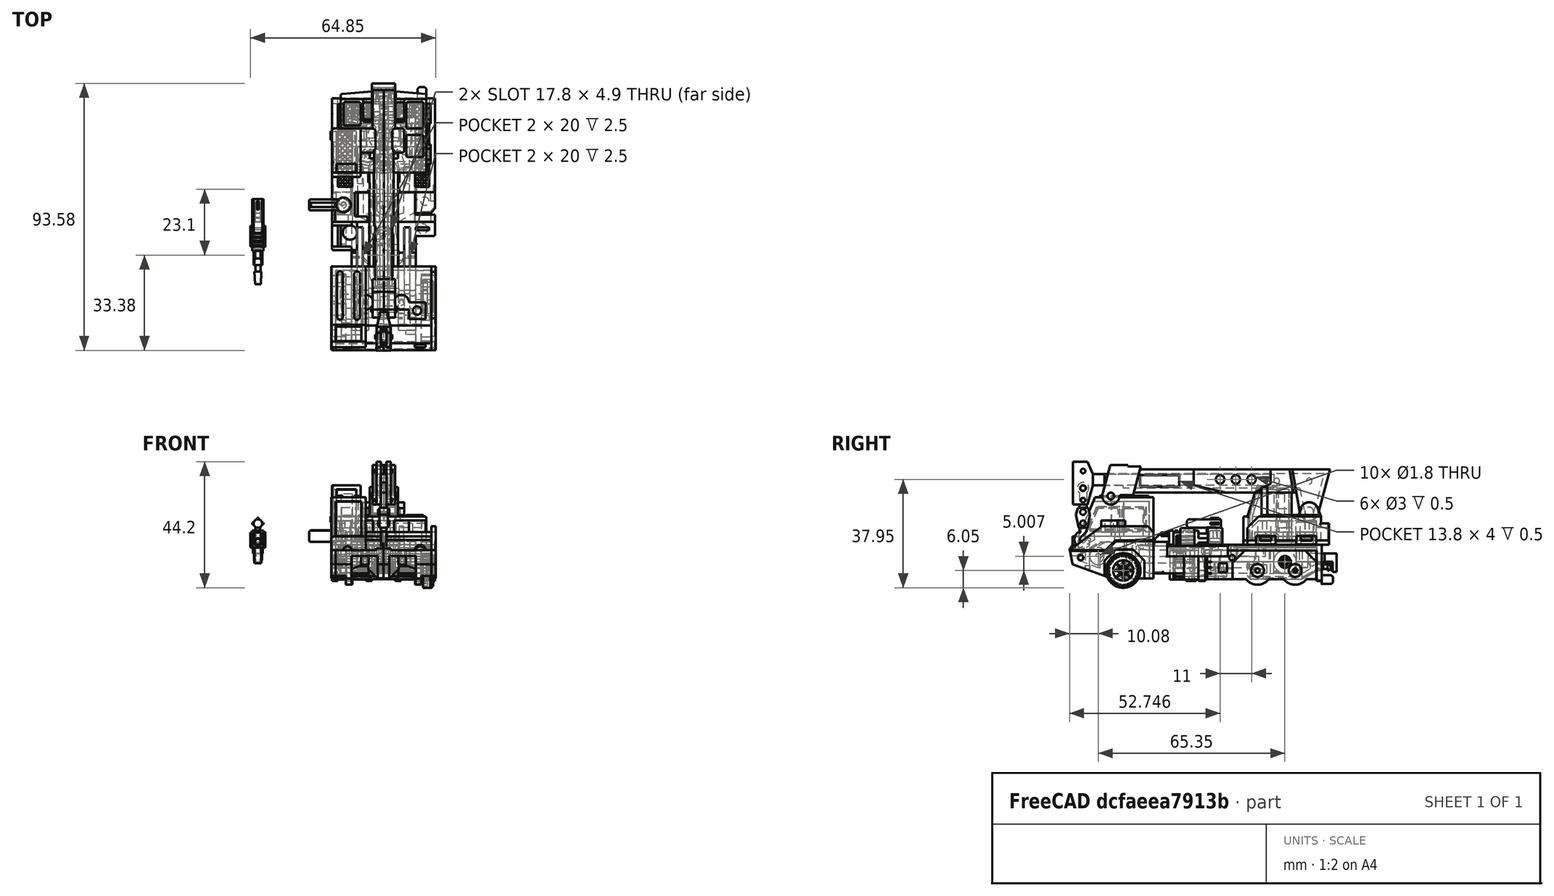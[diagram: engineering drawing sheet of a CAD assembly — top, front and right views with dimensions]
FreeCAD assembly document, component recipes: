
FREECAD ASSEMBLY — COMPONENT RECIPES ("Hook")

This assembly document has 27 components, labeled P0..P26 below (a component is one placed body or linked part). 27 of them carry a construction recipe — the FreeCAD feature program that regenerates the part from scratch, quoted from this document or its linked companion documents; the rest are supplied as boundary geometry only. No exploded tour is included for this assembly.
NOTE — document 5 of 5 of this assembly tour. The two overview renders and the header above are repeated from document 1; the component sections below continue where the previous document stopped.
COMPONENT P26 — recipe-attached ("Head", modeled in this document).
Construction recipe (the document's own serialized feature program — sketch geometry with constraints, then the solid features built on it; lengths are millimeters unless a unit is written):

FEATURE [Sketcher::SketchObject] Sketch190
  ArcFitTolerance = 1e-06
  AttachmentSupport = -> [XY_Plane013]
  FullyConstrained = true
  MakeInternals = false
  MapMode = 5
  sketch-geometry (4):
    g0: LineSegment StartX=0 StartY=0 StartZ=0 EndX=8 EndY=0 EndZ=0
    g1: LineSegment StartX=8 StartY=0 StartZ=0 EndX=8 EndY=10 EndZ=0
    g2: LineSegment StartX=8 StartY=10 StartZ=0 EndX=0 EndY=10 EndZ=0
    g3: LineSegment StartX=0 StartY=10 StartZ=0 EndX=0 EndY=0 EndZ=0
  constraints (11):
    c: Coincident(g0,g1)
    c: Coincident(g1,g2)
    c: Coincident(g2,g3)
    c: Coincident(g3,g0)
    c: Horizontal(g0)
    c: Horizontal(g2)
    c: Vertical(g1)
    c: Vertical(g3)
    c: Coincident(g0,g-1)
    c: DistanceX(g2,g2) = 8
    c: DistanceY(g3,g3) = 10
FEATURE [PartDesign::Pad] Pad127
  Direction = (0,0,1)
  Length = 3.5
  Length2 = 10
  Profile = -> Sketch190
  ReferenceAxis = -> Sketch190 [N_Axis]
  Refine = true
  Suppressed = false
  Type = 0
FEATURE [Sketcher::SketchObject] Sketch191
  ArcFitTolerance = 1e-06
  AttachmentSupport = -> [Pad127]
  ExternalGeometry = -> [Pad127]
  FullyConstrained = true
  MakeInternals = false
  MapMode = 5
  Placement = pos=(0,0,0) rot=(1,0,0;3.14159rad)
  sketch-geometry (4):
    g0: LineSegment StartX=0 StartY=0 StartZ=0 EndX=0 EndY=-1.4 EndZ=0
    g1: LineSegment StartX=0 StartY=-1.4 StartZ=0 EndX=8 EndY=-1.4 EndZ=0
    g2: LineSegment StartX=8 StartY=-1.4 StartZ=0 EndX=8 EndY=0 EndZ=0
    g3: LineSegment StartX=8 StartY=0 StartZ=0 EndX=0 EndY=0 EndZ=0
  constraints (11):
    c: Coincident(g0,g1)
    c: Coincident(g1,g2)
    c: Coincident(g2,g3)
    c: Coincident(g3,g0)
    c: Vertical(g0)
    c: Vertical(g2)
    c: Horizontal(g1)
    c: Horizontal(g3)
    c: Coincident(g0,g-1)
    c: PointOnObject(g1,g-3)
    c: DistanceY(g0,g0) = 1.4
FEATURE [PartDesign::Pad] Pad128
  BaseFeature = -> Pad127
  Direction = (0,0,-1)
  Length = 3.5
  Length2 = 10
  Profile = -> Sketch191
  ReferenceAxis = -> Sketch191 [N_Axis]
  Refine = true
  Suppressed = false
  Type = 0
FEATURE [Sketcher::SketchObject] Sketch192
  ArcFitTolerance = 1e-06
  AttachmentSupport = -> [Pad128]
  ExternalGeometry = -> [Pad128]
  FullyConstrained = true
  MakeInternals = false
  MapMode = 5
  Placement = pos=(0,0,0) rot=(0.57735,-0.57735,-0.57735;2.0944rad)
  sketch-geometry (2):
    g0: ArcOfCircle CenterX=-8.65 CenterY=0 CenterZ=0 NormalX=0 NormalY=0 NormalZ=1 AngleXU=0 Radius=1.35 StartAngle=0 EndAngle=3.14159
    g1: LineSegment StartX=-10 StartY=2e-16 StartZ=0 EndX=-7.3 EndY=0 EndZ=0
  constraints (6):
    c: Coincident(g0,g-4)
    c: PointOnObject(g0,g-4)
    c: PointOnObject(g0,g-4)
    c: Diameter(g0) = 2.7
    c: Coincident(g1,g0)
    c: Coincident(g1,g0)
FEATURE [PartDesign::Pad] Pad129
  BaseFeature = -> Pad128
  Direction = (-1,0,0)
  Length = 1.8
  Length2 = 10
  Profile = -> Sketch192
  ReferenceAxis = -> Sketch192 [N_Axis]
  Refine = true
  Suppressed = false
  Type = 0
FEATURE [Sketcher::SketchObject] Sketch193
  ArcFitTolerance = 1e-06
  AttachmentSupport = -> [Pad129]
  ExternalGeometry = -> [Pad129]
  FullyConstrained = true
  MakeInternals = false
  MapMode = 5
  Placement = pos=(8,0,0) rot=(0.57735,0.57735,0.57735;2.0944rad)
  sketch-geometry (2):
    g0: ArcOfCircle CenterX=8.65 CenterY=0 CenterZ=0 NormalX=0 NormalY=0 NormalZ=1 AngleXU=0 Radius=1.35 StartAngle=0 EndAngle=3.14159
    g1: LineSegment StartX=7.3 StartY=2e-16 StartZ=0 EndX=10 EndY=0 EndZ=0
  constraints (6):
    c: Coincident(g0,g-4)
    c: PointOnObject(g0,g-4)
    c: PointOnObject(g0,g-4)
    c: Coincident(g1,g0)
    c: Coincident(g1,g0)
    c: Diameter(g0) = 2.7
FEATURE [PartDesign::Pad] Pad130
  BaseFeature = -> Pad129
  Direction = (1,0,0)
  Length = 1.8
  Length2 = 10
  Profile = -> Sketch193
  ReferenceAxis = -> Sketch193 [N_Axis]
  Refine = true
  Suppressed = false
  Type = 0
FEATURE [PartDesign::Pocket] Pocket088
  BaseFeature = -> Pad130
  Direction = (0,0,-1)
  Length = 0.5
  Length2 = 5
  Profile = -> Pad130 [Face1]
  Refine = true
  Suppressed = false
  Type = 0
FEATURE [PartDesign::Pad] Pad131
  BaseFeature = -> Pocket088
  Direction = (-1,0,0)
  Length = 0.1
  Length2 = 10
  Profile = -> Pocket088 [Face2]
  Refine = true
  Suppressed = false
  Type = 0
FEATURE [PartDesign::Pad] Pad132
  BaseFeature = -> Pad131
  Direction = (1,0,0)
  Length = 0.1
  Length2 = 10
  Profile = -> Pad131 [Face5]
  Refine = true
  Suppressed = false
  Type = 0
FEATURE [Sketcher::SketchObject] Sketch195
  ArcFitTolerance = 1e-06
  AttachmentOffset = pos=(0,0,-2.2) rot=(0,0,1;0rad)
  AttachmentSupport = -> [Pad132]
  ExternalGeometry = -> [Pad132]
  FullyConstrained = true
  MakeInternals = false
  MapMode = 5
  Placement = pos=(0.4,0,0) rot=(0.57735,-0.57735,-0.57735;2.0944rad)
  sketch-geometry (2):
    g0: LineSegment StartX=-10 StartY=5.6939e-12 StartZ=0 EndX=-7.3 EndY=5.694e-12 EndZ=0
    g1: ArcOfCircle CenterX=-8.65 CenterY=1e-16 CenterZ=0 NormalX=0 NormalY=0 NormalZ=1 AngleXU=0 Radius=1.35 StartAngle=3.14159 EndAngle=6.28319
  constraints (5):
    c: Coincident(g0,g-3)
    c: Coincident(g0,g-3)
    c: Coincident(g1,g0)
    c: Coincident(g1,g0)
    c: PointOnObject(g1,g0)
FEATURE [PartDesign::Pad] Pad133
  BaseFeature = -> Pad132
  Direction = (-1,0,0)
  Length = 7.2
  Length2 = 10
  Profile = -> Sketch195
  ReferenceAxis = -> Sketch195 [N_Axis]
  Refine = true
  Reversed = true
  Suppressed = false
  Type = 0
FEATURE [Sketcher::SketchObject] Sketch196
  ArcFitTolerance = 1e-06
  AttachmentSupport = -> [Pad133]
  ExternalGeometry = -> [Pad133]
  FullyConstrained = true
  MakeInternals = false
  MapMode = 5
  Placement = pos=(0,0,0) rot=(1,0,0;3.14159rad)
  sketch-geometry (16):
    g0: LineSegment StartX=6.3 StartY=-6.73887 StartZ=0 EndX=6.3 EndY=-3.23887 EndZ=0
    g1: LineSegment StartX=6.3 StartY=-3.23887 StartZ=0 EndX=7.64681 EndY=-3.56312 EndZ=0
    g2: LineSegment StartX=7.8 StartY=-3.75756 StartZ=0 EndX=7.8 EndY=-5.95756 EndZ=0
    g3: LineSegment StartX=7.67952 StartY=-6.14107 StartZ=0 EndX=6.3 EndY=-6.73887 EndZ=0
    g4: ArcOfCircle CenterX=7.6 CenterY=-5.95756 CenterZ=0 NormalX=0 NormalY=0 NormalZ=1 AngleXU=0 Radius=0.2 StartAngle=5.1213 EndAngle=6.28319
    g5: GeomPoint [constr] X=7.8 Y=-6.08887 Z=0
    g6: ArcOfCircle CenterX=7.6 CenterY=-3.75756 CenterZ=0 NormalX=0 NormalY=0 NormalZ=1 AngleXU=0 Radius=0.2 StartAngle=1e-16 EndAngle=1.33454
    g7: GeomPoint [constr] X=7.8 Y=-3.6 Z=0
    g8: LineSegment StartX=1.7 StartY=-3.23887 StartZ=0 EndX=1.7 EndY=-6.73887 EndZ=0
    g9: LineSegment StartX=1.7 StartY=-6.73887 StartZ=0 EndX=0.320479 EndY=-6.14107 EndZ=0
    g10: LineSegment StartX=0.2 StartY=-5.95756 StartZ=0 EndX=0.2 EndY=-3.75756 EndZ=0
    g11: LineSegment StartX=0.353187 StartY=-3.56312 StartZ=0 EndX=1.7 EndY=-3.23887 EndZ=0
    g12: ArcOfCircle CenterX=0.4 CenterY=-5.95756 CenterZ=0 NormalX=0 NormalY=0 NormalZ=1 AngleXU=0 Radius=0.2 StartAngle=3.14159 EndAngle=4.30348
    g13: GeomPoint [constr] X=0.2 Y=-6.08887 Z=0
    g14: ArcOfCircle CenterX=0.4 CenterY=-3.75756 CenterZ=0 NormalX=0 NormalY=0 NormalZ=1 AngleXU=0 Radius=0.2 StartAngle=1.80706 EndAngle=3.14159
    g15: GeomPoint [constr] X=0.2 Y=-3.6 Z=0
  constraints (40):
    c: Vertical(g0)
    c: Coincident(g1,g0)
    c: Vertical(g2)
    c: Coincident(g3,g0)
    c: PointOnObject(g5,g2)
    c: PointOnObject(g5,g3)
    c: Tangent(g2,g4) = 1.5708
    c: Tangent(g3,g4) = 1.5708
    c: PointOnObject(g7,g1)
    c: PointOnObject(g7,g2)
    c: Tangent(g1,g6) = 1.5708
    c: Tangent(g2,g6) = 1.5708
    c: DistanceY(g0,g0) = 3.5
    c: DistanceY(g2,g2) = 2.2
    c: Radius(g4) = 0.2
    c: Radius(g6) = 0.2
    c: DistanceY(g0,g5) = 0.65
    c: DistanceX(g0,g2) = 1.5
    c: DistanceX(g2,g-3) = 0.3
    c: DistanceY(g7,g-3) = 2.2
    c: Vertical(g8)
    c: Coincident(g9,g8)
    c: Vertical(g10)
    c: Coincident(g11,g8)
    c: DistanceY(g8,g8) = 3.5
    c: PointOnObject(g13,g9)
    c: PointOnObject(g13,g10)
    c: Tangent(g9,g12) = 1.5708
    c: Tangent(g10,g12) = 1.5708
    c: PointOnObject(g15,g10)
    c: PointOnObject(g15,g11)
    c: Tangent(g10,g14) = 1.5708
    c: Tangent(g11,g14) = 1.5708
    c: DistanceX(g-4,g10) = 0.3
    c: Radius(g14) = 0.2
    c: Radius(g12) = 0.2
    c: DistanceX(g10,g8) = 1.5
    c: DistanceY(g8,g13) = 0.65
    c: DistanceY(g15,g-4) = 2.2
    c: DistanceY(g10,g10) = 2.2
FEATURE [PartDesign::Pad] Pad134
  BaseFeature = -> Pad133
  Direction = (0,0,-1)
  Length = 0.8
  Length2 = 10
  Profile = -> Sketch196
  ReferenceAxis = -> Sketch196 [N_Axis]
  Refine = true
  Suppressed = false
  Type = 0
FEATURE [Sketcher::SketchObject] Sketch197
  ArcFitTolerance = 1e-06
  AttachmentSupport = -> [Pad134]
  ExternalGeometry = -> [Pad134]
  FullyConstrained = true
  MakeInternals = false
  MapMode = 5
  Placement = pos=(0,0,0) rot=(1,0,0;3.14159rad)
  sketch-geometry (4):
    g0: LineSegment StartX=0.8 StartY=-1.4 StartZ=0 EndX=0.8 EndY=-7.3 EndZ=0
    g1: LineSegment StartX=0.8 StartY=-7.3 StartZ=0 EndX=7.2 EndY=-7.3 EndZ=0
    g2: LineSegment StartX=7.2 StartY=-7.3 StartZ=0 EndX=7.2 EndY=-1.4 EndZ=0
    g3: LineSegment StartX=7.2 StartY=-1.4 StartZ=0 EndX=0.8 EndY=-1.4 EndZ=0
  constraints (13):
    c: Coincident(g0,g1)
    c: Coincident(g1,g2)
    c: Coincident(g2,g3)
    c: Coincident(g3,g0)
    c: Vertical(g0)
    c: Vertical(g2)
    c: Horizontal(g1)
    c: Horizontal(g3)
    c: DistanceX(g3,g3) = 6.4
    c: DistanceX(g-3,g-3) = 8.2
    c: DistanceX(g-3,g0) = 0.9
    c: PointOnObject(g2,g-3)
    c: PointOnObject(g1,g-4)
FEATURE [PartDesign::Pad] Pad135
  BaseFeature = -> Pad134
  Direction = (0,0,-1)
  Length = 0.5
  Length2 = 10
  Profile = -> Sketch197
  ReferenceAxis = -> Sketch197 [N_Axis]
  Refine = true
  Suppressed = false
  Type = 0
FEATURE [Sketcher::SketchObject] Sketch198
  ArcFitTolerance = 1e-06
  AttachmentSupport = -> [Pad135]
  ExternalGeometry = -> [Pad135]
  FullyConstrained = true
  MakeInternals = false
  MapMode = 5
  Placement = pos=(0,0,-0.5) rot=(1,0,0;3.14159rad)
  sketch-geometry (8):
    g0: LineSegment StartX=5.75 StartY=-4.7 StartZ=0 EndX=5.75 EndY=-7.3 EndZ=0
    g1: LineSegment StartX=5.75 StartY=-7.3 StartZ=0 EndX=6.65 EndY=-7.3 EndZ=0
    g2: LineSegment StartX=6.65 StartY=-7.3 StartZ=0 EndX=6.65 EndY=-4.7 EndZ=0
    g3: LineSegment StartX=6.65 StartY=-4.7 StartZ=0 EndX=5.75 EndY=-4.7 EndZ=0
    g4: LineSegment StartX=2.25 StartY=-4.7 StartZ=0 EndX=1.35 EndY=-4.7 EndZ=0
    g5: LineSegment StartX=1.35 StartY=-4.7 StartZ=0 EndX=1.35 EndY=-7.3 EndZ=0
    g6: LineSegment StartX=1.35 StartY=-7.3 StartZ=0 EndX=2.25 EndY=-7.3 EndZ=0
    g7: LineSegment StartX=2.25 StartY=-7.3 StartZ=0 EndX=2.25 EndY=-4.7 EndZ=0
  constraints (25):
    c: Coincident(g0,g1)
    c: Coincident(g1,g2)
    c: Coincident(g2,g3)
    c: Coincident(g3,g0)
    c: Vertical(g0)
    c: Vertical(g2)
    c: Horizontal(g1)
    c: Horizontal(g3)
    c: DistanceX(g3,g3) = 0.9
    c: DistanceY(g0,g0) = 2.6
    c: PointOnObject(g1,g-4)
    c: DistanceX(g1,g-4) = 0.55
    c: DistanceX(g-4,g-4) = 6.4
    c: Coincident(g4,g5)
    c: Coincident(g5,g6)
    c: Coincident(g6,g7)
    c: Coincident(g7,g4)
    c: Horizontal(g4)
    c: Horizontal(g6)
    c: Vertical(g5)
    c: Vertical(g7)
    c: DistanceX(g4,g4) = 0.9
    c: DistanceY(g7,g7) = 2.6
    c: PointOnObject(g6,g-4)
    c: DistanceX(g-4,g5) = 0.55
FEATURE [PartDesign::Pad] Pad136
  BaseFeature = -> Pad135
  Direction = (0,0,-1)
  Length = 2.5
  Length2 = 10
  Profile = -> Sketch198
  ReferenceAxis = -> Sketch198 [N_Axis]
  Refine = true
  Suppressed = false
  Type = 0
FEATURE [Sketcher::SketchObject] Sketch199
  ArcFitTolerance = 1e-06
  AttachmentSupport = -> [Pad136]
  ExternalGeometry = -> [Pad136]
  FullyConstrained = true
  MakeInternals = false
  MapMode = 5
  Placement = pos=(6.65,0,0) rot=(0.57735,0.57735,0.57735;2.0944rad)
  sketch-geometry (3):
    g0: LineSegment StartX=4.7 StartY=-3 StartZ=0 EndX=5.2 EndY=-3 EndZ=0
    g1: LineSegment StartX=5.2 StartY=-3 StartZ=0 EndX=4.7 EndY=-0.8 EndZ=0
    g2: LineSegment StartX=4.7 StartY=-0.8 StartZ=0 EndX=4.7 EndY=-3 EndZ=0
  constraints (7):
    c: Coincident(g0,g-4)
    c: PointOnObject(g0,g-4)
    c: Coincident(g1,g0)
    c: Coincident(g1,g-3)
    c: Coincident(g2,g1)
    c: Coincident(g2,g0)
    c: DistanceX(g0,g0) = 0.5
FEATURE [PartDesign::Pocket] Pocket089
  BaseFeature = -> Pad136
  Direction = (-1,0,0)
  Length = 5.3
  Length2 = 5
  Profile = -> Sketch199
  ReferenceAxis = -> Sketch199 [N_Axis]
  Refine = true
  Suppressed = false
  Type = 0
FEATURE [Sketcher::SketchObject] Sketch200
  ArcFitTolerance = 1e-06
  AttachmentSupport = -> [Pocket089]
  ExternalGeometry = -> [Pocket089]
  FullyConstrained = true
  MakeInternals = false
  MapMode = 5
  Placement = pos=(0,0,-0.5) rot=(1,0,0;3.14159rad)
  sketch-geometry (4):
    g0: LineSegment StartX=1.7 StartY=-3.23887 StartZ=0 EndX=6.3 EndY=-3.23887 EndZ=0
    g1: LineSegment StartX=6.3 StartY=-3.23887 StartZ=0 EndX=6.3 EndY=-2.73887 EndZ=0
    g2: LineSegment StartX=6.3 StartY=-2.73887 StartZ=0 EndX=1.7 EndY=-2.73887 EndZ=0
    g3: LineSegment StartX=1.7 StartY=-2.73887 StartZ=0 EndX=1.7 EndY=-3.23887 EndZ=0
  constraints (10):
    c: Coincident(g0,g1)
    c: Coincident(g1,g2)
    c: Coincident(g2,g3)
    c: Coincident(g3,g0)
    c: Horizontal(g2)
    c: Vertical(g1)
    c: Vertical(g3)
    c: DistanceY(g3,g3) = 0.5
    c: Coincident(g0,g-5)
    c: Coincident(g0,g-4)
FEATURE [PartDesign::Pad] Pad137
  BaseFeature = -> Pocket089
  Direction = (0,0,-1)
  Length = 2.5
  Length2 = 10
  Profile = -> Sketch200
  ReferenceAxis = -> Sketch200 [N_Axis]
  Refine = true
  Suppressed = false
  Type = 0
FEATURE [Sketcher::SketchObject] Sketch201
  ArcFitTolerance = 1e-06
  AttachmentSupport = -> [Pad137]
  ExternalGeometry = -> [Pad137]
  FullyConstrained = true
  MakeInternals = false
  MapMode = 5
  Placement = pos=(1.26509e-11,3.23887,0) rot=(0,0.707107,0.707107;3.14159rad)
  sketch-geometry (6):
    g0: LineSegment StartX=-1.7 StartY=-3 StartZ=0 EndX=-2.2 EndY=-3 EndZ=0
    g1: LineSegment StartX=-6.3 StartY=-3 StartZ=0 EndX=-5.8 EndY=-3 EndZ=0
    g2: LineSegment StartX=-6.3 StartY=-3 StartZ=0 EndX=-6.3 EndY=-0.5 EndZ=0
    g3: LineSegment StartX=-1.7 StartY=-3 StartZ=0 EndX=-1.7 EndY=-0.5 EndZ=0
    g4: LineSegment StartX=-1.7 StartY=-0.5 StartZ=0 EndX=-2.2 EndY=-3 EndZ=0
    g5: LineSegment StartX=-5.8 StartY=-3 StartZ=0 EndX=-6.3 EndY=-0.5 EndZ=0
  constraints (15):
    c: DistanceX(g-3,g-3) = 4.6
    c: Coincident(g0,g-5)
    c: PointOnObject(g0,g-3)
    c: Coincident(g1,g-4)
    c: PointOnObject(g1,g-3)
    c: Coincident(g2,g1)
    c: Coincident(g2,g-6)
    c: Coincident(g3,g0)
    c: Coincident(g3,g-6)
    c: Coincident(g4,g3)
    c: Coincident(g4,g0)
    c: Coincident(g5,g1)
    c: Coincident(g5,g2)
    c: DistanceX(g0,g0) = 0.5
    c: DistanceX(g1,g1) = 0.5
FEATURE [PartDesign::Pocket] Pocket090
  BaseFeature = -> Pad137
  Direction = (-3.906e-12,-1,2e-16)
  Length = 0.5
  Length2 = 5
  Profile = -> Sketch201
  ReferenceAxis = -> Sketch201 [N_Axis]
  Refine = true
  Suppressed = false
  Type = 0
FEATURE [Sketcher::SketchObject] Sketch202
  ArcFitTolerance = 1e-06
  AttachmentSupport = -> [Pocket090]
  ExternalGeometry = -> [Pocket090]
  FullyConstrained = true
  MakeInternals = false
  MapMode = 5
  Placement = pos=(0,0,-0.5) rot=(1,0,0;3.14159rad)
  sketch-geometry (4):
    g0: LineSegment StartX=1.7 StartY=-2.73887 StartZ=0 EndX=6.3 EndY=-2.73887 EndZ=0
    g1: LineSegment StartX=6.3 StartY=-2.73887 StartZ=0 EndX=5.8 EndY=-1.4 EndZ=0
    g2: LineSegment StartX=1.7 StartY=-2.73887 StartZ=0 EndX=2.2 EndY=-1.4 EndZ=0
    g3: LineSegment StartX=2.2 StartY=-1.4 StartZ=0 EndX=5.8 EndY=-1.4 EndZ=0
  constraints (12):
    c: Coincident(g0,g-4)
    c: Coincident(g0,g-3)
    c: Coincident(g1,g-3)
    c: PointOnObject(g1,g-5)
    c: Coincident(g2,g-4)
    c: PointOnObject(g2,g-5)
    c: Coincident(g3,g2)
    c: Coincident(g3,g1)
    c: DistanceX(g-4,g-3) = 3.6
    c: DistanceX(g2,g1) = 3.6
    c: DistanceX(g0,g0) = 4.6
    c: DistanceX(g0,g2) = 0.5
FEATURE [PartDesign::Pad] Pad138
  BaseFeature = -> Pocket090
  Direction = (0,0,-1)
  Length = 2.25
  Length2 = 10
  Profile = -> Sketch202
  ReferenceAxis = -> Sketch202 [N_Axis]
  Refine = true
  Suppressed = false
  Type = 0
FEATURE [Sketcher::SketchObject] Sketch203
  ArcFitTolerance = 1e-06
  AttachmentSupport = -> [Pad138]
  ExternalGeometry = -> [Pad138]
  FullyConstrained = true
  MakeInternals = false
  MapMode = 5
  Placement = pos=(9.9689e-12,2.73887,0) rot=(0,0.707107,0.707107;3.14159rad)
  sketch-geometry (6):
    g0: LineSegment StartX=-1.7 StartY=-0.5 StartZ=0 EndX=-1.7 EndY=-2.75 EndZ=0
    g1: LineSegment StartX=-1.7 StartY=-2.75 StartZ=0 EndX=-2.15 EndY=-2.75 EndZ=0
    g2: LineSegment StartX=-2.15 StartY=-2.75 StartZ=0 EndX=-1.7 EndY=-0.5 EndZ=0
    g3: LineSegment StartX=-5.85 StartY=-2.75 StartZ=0 EndX=-6.3 EndY=-2.75 EndZ=0
    g4: LineSegment StartX=-6.3 StartY=-2.75 StartZ=0 EndX=-6.3 EndY=-0.5 EndZ=0
    g5: LineSegment StartX=-6.3 StartY=-0.5 StartZ=0 EndX=-5.85 EndY=-2.75 EndZ=0
  constraints (12):
    c: Coincident(g0,g-4)
    c: Coincident(g0,g-4)
    c: Coincident(g1,g0)
    c: Coincident(g1,g-3)
    c: Coincident(g2,g1)
    c: Coincident(g2,g0)
    c: Coincident(g3,g-5)
    c: Coincident(g3,g-6)
    c: Coincident(g4,g3)
    c: Coincident(g4,g-6)
    c: Coincident(g5,g4)
    c: Coincident(g5,g3)
FEATURE [PartDesign::Pocket] Pocket091
  BaseFeature = -> Pad138
  Direction = (-3.6398e-12,-1,2e-16)
  Length = 1.3
  Length2 = 5
  Profile = -> Sketch203
  ReferenceAxis = -> Sketch203 [N_Axis]
  Refine = true
  Suppressed = false
  Type = 0
FEATURE [Sketcher::SketchObject] Sketch204
  ArcFitTolerance = 1e-06
  AttachmentSupport = -> [Pocket091]
  ExternalGeometry = -> [Pocket091]
  FullyConstrained = true
  MakeInternals = false
  MapMode = 5
  Placement = pos=(7.2,0,0) rot=(0.57735,0.57735,0.57735;2.0944rad)
  sketch-geometry (3):
    g0: LineSegment StartX=2.3 StartY=-2.75 StartZ=0 EndX=1.4 EndY=-2.75 EndZ=0
    g1: LineSegment StartX=1.4 StartY=-2.75 StartZ=0 EndX=1.4 EndY=-0.5 EndZ=0
    g2: LineSegment StartX=2.3 StartY=-2.75 StartZ=0 EndX=1.4 EndY=-0.5 EndZ=0
  constraints (7):
    c: PointOnObject(g0,g-4)
    c: Coincident(g0,g-6)
    c: Coincident(g1,g0)
    c: Coincident(g1,g-3)
    c: Coincident(g2,g0)
    c: Coincident(g2,g1)
    c: DistanceX(g0,g0) = 0.9
FEATURE [PartDesign::Pocket] Pocket092
  BaseFeature = -> Pocket091
  Direction = (-1,0,0)
  Length = 6
  Length2 = 5
  Profile = -> Sketch204
  ReferenceAxis = -> Sketch204 [N_Axis]
  Refine = true
  Suppressed = false
  Type = 0
FEATURE [Sketcher::SketchObject] Sketch205
  ArcFitTolerance = 1e-06
  AttachmentOffset = pos=(0,0,-2.35) rot=(0,0,1;0rad)
  AttachmentSupport = -> [Pocket092]
  ExternalGeometry = -> [Pocket092]
  FullyConstrained = true
  MakeInternals = false
  MapMode = 5
  Placement = pos=(4.85,0,0) rot=(0.57735,0.57735,0.57735;2.0944rad)
  sketch-geometry (3):
    g0: ArcOfCircle CenterX=1.61334 CenterY=-2.02302 CenterZ=0 NormalX=0 NormalY=0 NormalZ=1 AngleXU=0 Radius=1 StartAngle=4.4974 EndAngle=5.46927
    g1: LineSegment StartX=2.3 StartY=-2.75 StartZ=0 EndX=1.4 EndY=-0.5 EndZ=0
    g2: LineSegment StartX=1.4 StartY=-0.5 StartZ=0 EndX=1.4 EndY=-3 EndZ=0
  constraints (8):
    c: Coincident(g0,g-3)
    c: PointOnObject(g0,g-4)
    c: Coincident(g1,g0)
    c: Coincident(g1,g-5)
    c: Coincident(g2,g1)
    c: Coincident(g2,g0)
    c: Radius(g0) = 1
    c: DistanceY(g-6,g0) = 0
FEATURE [PartDesign::Pad] Pad139
  BaseFeature = -> Pocket092
  Direction = (1,0,0)
  Length = 1.7
  Length2 = 10
  Profile = -> Sketch205
  ReferenceAxis = -> Sketch205 [N_Axis]
  Refine = true
  Reversed = true
  Suppressed = false
  Type = 0
FEATURE [PartDesign::Fillet] Fillet008
  Base = -> Pad139 [Edge33,Edge34,Edge30,Edge45,Edge44,Edge6,Edge8,Edge1,Edge2]
  BaseFeature = -> Pad139
  Radius = 0.2
  Refine = true
  SupportTransform = false
  Suppressed = false
  UseAllEdges = false
FEATURE [Sketcher::SketchObject] Sketch206
  ArcFitTolerance = 1e-06
  AttachmentSupport = -> [Fillet008]
  ExternalGeometry = -> [Fillet008]
  FullyConstrained = true
  MakeInternals = false
  MapMode = 5
  Placement = pos=(0,0,-0.8) rot=(1,0,0;3.14159rad)
  sketch-geometry (8):
    g0: LineSegment StartX=1.35 StartY=-3.52885 StartZ=0 EndX=0.4 EndY=-3.75756 EndZ=0
    g1: LineSegment StartX=0.4 StartY=-3.75756 StartZ=0 EndX=0.4 EndY=-5.95756 EndZ=0
    g2: LineSegment StartX=0.4 StartY=-5.95756 StartZ=0 EndX=1.35 EndY=-6.36923 EndZ=0
    g3: LineSegment StartX=1.35 StartY=-3.52885 StartZ=0 EndX=1.35 EndY=-6.36923 EndZ=0
    g4: LineSegment StartX=7.6 StartY=-3.75756 StartZ=0 EndX=7.6 EndY=-5.95756 EndZ=0
    g5: LineSegment StartX=7.6 StartY=-5.95756 StartZ=0 EndX=6.65 EndY=-6.36923 EndZ=0
    g6: LineSegment StartX=7.6 StartY=-3.75756 StartZ=0 EndX=6.65 EndY=-3.52885 EndZ=0
    g7: LineSegment StartX=6.65 StartY=-3.52885 StartZ=0 EndX=6.65 EndY=-6.36923 EndZ=0
  constraints (20):
    c: Coincident(g1,g0)
    c: Coincident(g2,g1)
    c: Coincident(g3,g0)
    c: Coincident(g3,g2)
    c: Vertical(g3)
    c: Parallel(g0,g-3)
    c: Parallel(g2,g-7)
    c: PointOnObject(g-10,g3)
    c: Coincident(g-8,g1)
    c: Coincident(g0,g-9)
    c: Coincident(g4,g-16)
    c: Coincident(g4,g-15)
    c: Coincident(g5,g4)
    c: PointOnObject(g5,g-17)
    c: Coincident(g6,g4)
    c: Coincident(g7,g6)
    c: Coincident(g7,g5)
    c: Vertical(g7)
    c: Parallel(g-11,g6)
    c: Parallel(g5,g-14)
FEATURE [PartDesign::Pocket] Pocket093
  BaseFeature = -> Fillet008
  Direction = (0,0,1)
  Length = 0.3
  Length2 = 5
  Profile = -> Sketch206
  ReferenceAxis = -> Sketch206 [N_Axis]
  Refine = true
  Suppressed = false
  Type = 0
FEATURE [PartDesign::SubShapeBinder] Binder008
  BindCopyOnChange = 0
  BindMode = 2
  ClaimChildren = false
  Context = -> Part [Body014.Binder008.]
  Fuse = false
  MakeFace = true
  OffsetFill = false
  OffsetIntersection = false
  OffsetJoinType = 0
  OffsetOpenResult = false
  PartialLoad = false
  Refine = true
  Relative = true
  _Version = 2
FEATURE [Sketcher::SketchObject] Sketch207
  ArcFitTolerance = 1e-06
  AttachmentSupport = -> [Binder008]
  ExternalGeometry = -> [Binder008]
  FullyConstrained = true
  MakeInternals = false
  MapMode = 5
  Placement = pos=(0,0,-4.5) rot=(1,0,0;3.14159rad)
  sketch-geometry (4):
    g0: LineSegment StartX=20.3 StartY=-45.2611 StartZ=0 EndX=20.3 EndY=-43.8 EndZ=0
    g1: LineSegment StartX=20.3 StartY=-43.8 StartZ=0 EndX=15.7 EndY=-43.8 EndZ=0
    g2: LineSegment StartX=15.7 StartY=-43.8 StartZ=0 EndX=15.7 EndY=-45.2611 EndZ=0
    g3: LineSegment StartX=15.7 StartY=-45.2611 StartZ=0 EndX=20.3 EndY=-45.2611 EndZ=0
  constraints (10):
    c: Coincident(g0,g1)
    c: Coincident(g1,g2)
    c: Coincident(g2,g3)
    c: Coincident(g3,g0)
    c: Vertical(g0)
    c: Vertical(g2)
    c: Horizontal(g1)
    c: Horizontal(g3)
    c: Coincident(g0,g-8)
    c: Coincident(g1,g-10)
FEATURE [PartDesign::Pad] Pad140
  Direction = (0,0,-1)
  Length = 2
  Length2 = 10
  Profile = -> Sketch207
  ReferenceAxis = -> Sketch207 [N_Axis]
  Refine = true
  Suppressed = false
  Type = 0
FEATURE [Sketcher::SketchObject] Sketch208
  ArcFitTolerance = 1e-06
  AttachmentSupport = -> [Pad140]
  ExternalGeometry = -> [Pad140]
  FullyConstrained = true
  MakeInternals = false
  MapMode = 5
  Placement = pos=(0,43.8,0) rot=(1,0,0;1.5708rad)
  sketch-geometry (6):
    g0: LineSegment StartX=15.7 StartY=-6.5 StartZ=0 EndX=15.7 EndY=-4.5 EndZ=0
    g1: LineSegment StartX=16.25 StartY=-6.5 StartZ=0 EndX=15.7 EndY=-4.5 EndZ=0
    g2: LineSegment StartX=20.3 StartY=-4.5 StartZ=0 EndX=19.75 EndY=-6.5 EndZ=0
    g3: LineSegment StartX=15.7 StartY=-6.5 StartZ=0 EndX=16.25 EndY=-6.5 EndZ=0
    g4: LineSegment StartX=19.75 StartY=-6.5 StartZ=0 EndX=20.3 EndY=-6.5 EndZ=0
    g5: LineSegment StartX=20.3 StartY=-6.5 StartZ=0 EndX=20.3 EndY=-4.5 EndZ=0
  constraints (15):
    c: Coincident(g0,g-4)
    c: Coincident(g1,g0)
    c: DistanceX(g-3,g-3) = 4.6
    c: Coincident(g3,g0)
    c: Coincident(g3,g1)
    c: Horizontal(g3)
    c: Coincident(g4,g2)
    c: Coincident(g4,g-5)
    c: Horizontal(g4)
    c: Coincident(g5,g4)
    c: Coincident(g5,g2)
    c: DistanceX(g4,g4) = 0.55
    c: DistanceX(g3,g3) = 0.55
    c: Coincident(g2,g-5)
    c: Coincident(g0,g-4)
FEATURE [PartDesign::Pocket] Pocket094
  BaseFeature = -> Pad140
  Direction = (0,1,-2e-16)
  Length = 5
  Length2 = 5
  Profile = -> Sketch208
  ReferenceAxis = -> Sketch208 [N_Axis]
  Refine = true
  Suppressed = false
  Type = 0
FEATURE [Sketcher::SketchObject] Sketch209
  ArcFitTolerance = 1e-06
  AttachmentOffset = pos=(0,0,-2) rot=(0,0,1;0rad)
  AttachmentSupport = -> [Pocket094]
  ExternalGeometry = -> [Pocket094]
  FullyConstrained = true
  MakeInternals = false
  MapMode = 5
  Placement = pos=(0,0,-4.5) rot=(1,0,0;3.14159rad)
  sketch-geometry (6):
    g0: LineSegment StartX=19.55 StartY=-43.8 StartZ=0 EndX=16.45 EndY=-43.8 EndZ=0
    g1: LineSegment StartX=16.45 StartY=-43.8 StartZ=0 EndX=16.6 EndY=-41.6 EndZ=0
    g2: LineSegment StartX=16.6 StartY=-41.6 StartZ=0 EndX=16.9 EndY=-41.25 EndZ=0
    g3: LineSegment StartX=16.9 StartY=-41.25 StartZ=0 EndX=19.1 EndY=-41.25 EndZ=0
    g4: LineSegment StartX=19.1 StartY=-41.25 StartZ=0 EndX=19.4 EndY=-41.6 EndZ=0
    g5: LineSegment StartX=19.4 StartY=-41.6 StartZ=0 EndX=19.55 EndY=-43.8 EndZ=0
  constraints (18):
    c: PointOnObject(g0,g-3)
    c: PointOnObject(g0,g-3)
    c: DistanceX(g0,g-3) = 0.2
    c: DistanceX(g-3,g0) = 0.2
    c: Coincident(g1,g0)
    c: Coincident(g2,g1)
    c: Coincident(g3,g2)
    c: Horizontal(g3)
    c: Coincident(g4,g3)
    c: Coincident(g5,g4)
    c: Coincident(g5,g0)
    c: DistanceX(g-3,g1) = 0.35
    c: DistanceX(g4,g-3) = 0.35
    c: DistanceY(g0,g1) = 2.2
    c: DistanceY(g0,g4) = 2.2
    c: DistanceY(g4,g3) = 0.35
    c: DistanceX(g3,g4) = 0.3
    c: DistanceX(g1,g2) = 0.3
FEATURE [PartDesign::Pad] Pad141
  BaseFeature = -> Pocket094
  Direction = (0,0,-1)
  Length = 1.8
  Length2 = 10
  Profile = -> Sketch209
  ReferenceAxis = -> Sketch209 [N_Axis]
  Refine = true
  Suppressed = false
  Type = 0
FEATURE [Sketcher::SketchObject] Sketch210
  ArcFitTolerance = 1e-06
  AttachmentSupport = -> [Pad141]
  ExternalGeometry = -> [Pad141]
  FullyConstrained = true
  MakeInternals = false
  MapMode = 5
  Placement = pos=(0,0,-6.3) rot=(1,0,0;3.14159rad)
  sketch-geometry (8):
    g0: LineSegment StartX=18.3 StartY=-42.3 StartZ=0 EndX=18.3 EndY=-42.2 EndZ=0
    g1: LineSegment StartX=18.3 StartY=-42.2 StartZ=0 EndX=17.7 EndY=-42.2 EndZ=0
    g2: LineSegment StartX=17.7 StartY=-42.2 StartZ=0 EndX=17.7 EndY=-42.3 EndZ=0
    g3: LineSegment StartX=17.7 StartY=-42.3 StartZ=0 EndX=18.3 EndY=-42.3 EndZ=0
    g4: LineSegment StartX=18.3 StartY=-42.1 StartZ=0 EndX=18.3 EndY=-42 EndZ=0
    g5: LineSegment StartX=18.3 StartY=-42 StartZ=0 EndX=17.7 EndY=-42 EndZ=0
    g6: LineSegment StartX=17.7 StartY=-42 StartZ=0 EndX=17.7 EndY=-42.1 EndZ=0
    g7: LineSegment StartX=17.7 StartY=-42.1 StartZ=0 EndX=18.3 EndY=-42.1 EndZ=0
  constraints (25):
    c: Coincident(g0,g1)
    c: Coincident(g1,g2)
    c: Coincident(g2,g3)
    c: Coincident(g3,g0)
    c: Vertical(g0)
    c: Vertical(g2)
    c: Horizontal(g1)
    c: Horizontal(g3)
    c: Coincident(g4,g5)
    c: Coincident(g5,g6)
    c: Coincident(g6,g7)
    c: Coincident(g7,g4)
    c: Vertical(g4)
    c: Vertical(g6)
    c: Horizontal(g5)
    c: Horizontal(g7)
    c: DistanceX(g3,g3) = 0.6
    c: DistanceX(g5,g5) = 0.6
    c: DistanceX(g6,g1) = 0
    c: DistanceY(g1,g6) = 0.1
    c: DistanceY(g2,g2) = 0.1
    c: DistanceY(g6,g6) = 0.1
    c: DistanceX(g-3,g5) = 1.1
    c: DistanceX(g4,g-4) = 1.1
    c: DistanceY(g5,g-3) = 0.4
FEATURE [PartDesign::Pad] Pad142
  BaseFeature = -> Pad141
  Direction = (0,0,-1)
  Length = 0.2
  Length2 = 10
  Profile = -> Sketch210
  ReferenceAxis = -> Sketch210 [N_Axis]
  Refine = true
  Suppressed = false
  Type = 0
FEATURE [Sketcher::SketchObject] Sketch211
  ArcFitTolerance = 1e-06
  AttachmentSupport = -> [Pad142]
  ExternalGeometry = -> [Pad142]
  FullyConstrained = true
  MakeInternals = false
  MapMode = 5
  Placement = pos=(0,0,-6.3) rot=(1,0,0;3.14159rad)
  sketch-geometry (4):
    g0: LineSegment StartX=18.3 StartY=-43.8 StartZ=0 EndX=18.3 EndY=-43 EndZ=0
    g1: LineSegment StartX=18.3 StartY=-43 StartZ=0 EndX=17.7 EndY=-43 EndZ=0
    g2: LineSegment StartX=17.7 StartY=-43 StartZ=0 EndX=17.7 EndY=-43.8 EndZ=0
    g3: LineSegment StartX=17.7 StartY=-43.8 StartZ=0 EndX=18.3 EndY=-43.8 EndZ=0
  constraints (13):
    c: Coincident(g0,g1)
    c: Coincident(g1,g2)
    c: Coincident(g2,g3)
    c: Coincident(g3,g0)
    c: Vertical(g0)
    c: Vertical(g2)
    c: Horizontal(g1)
    c: Horizontal(g3)
    c: PointOnObject(g0,g-3)
    c: DistanceX(g1,g1) = 0.6
    c: DistanceY(g2,g2) = 0.8
    c: DistanceX(g-5,g2) = 1.25
    c: DistanceX(g0,g-4) = 1.25
FEATURE [PartDesign::Pad] Pad143
  BaseFeature = -> Pad142
  Direction = (0,0,-1)
  Length = 0.5
  Length2 = 10
  Profile = -> Sketch211
  ReferenceAxis = -> Sketch211 [N_Axis]
  Refine = true
  Suppressed = false
  Type = 0
FEATURE [Sketcher::SketchObject] Sketch212
  ArcFitTolerance = 1e-06
  AttachmentSupport = -> [Pad143]
  ExternalGeometry = -> [Pad143]
  FullyConstrained = true
  MakeInternals = false
  MapMode = 5
  Placement = pos=(17.7,0,0) rot=(0.57735,-0.57735,-0.57735;2.0944rad)
  sketch-geometry (3):
    g0: LineSegment StartX=-43.8 StartY=-6.5 StartZ=0 EndX=-43.2 EndY=-6.8 EndZ=0
    g1: LineSegment StartX=-43.2 StartY=-6.8 StartZ=0 EndX=-43.8 EndY=-6.8 EndZ=0
    g2: LineSegment StartX=-43.8 StartY=-6.8 StartZ=0 EndX=-43.8 EndY=-6.5 EndZ=0
  constraints (7):
    c: Coincident(g0,g-3)
    c: PointOnObject(g0,g-4)
    c: Coincident(g1,g0)
    c: Coincident(g1,g-4)
    c: Coincident(g2,g1)
    c: Coincident(g2,g0)
    c: DistanceX(g0,g-4) = 0.2
FEATURE [PartDesign::Pocket] Pocket095
  BaseFeature = -> Pad143
  Direction = (1,0,0)
  Length = 1
  Length2 = 5
  Profile = -> Sketch212
  ReferenceAxis = -> Sketch212 [N_Axis]
  Refine = true
  Suppressed = false
  Type = 0
FEATURE [Sketcher::SketchObject] Sketch342
  ArcFitTolerance = 1e-06
  AttachmentSupport = -> [Pocket093]
  ExternalGeometry = -> [Pocket093]
  FullyConstrained = true
  MakeInternals = false
  MapMode = 5
  Placement = pos=(-0.1,0,0) rot=(0.57735,-0.57735,-0.57735;2.0944rad)
  sketch-geometry (4):
    g0: LineSegment StartX=-7.3 StartY=0 StartZ=0 EndX=-4.3 EndY=0 EndZ=0
    g1: LineSegment StartX=-4.3 StartY=0 StartZ=0 EndX=-4.3 EndY=3 EndZ=0
    g2: LineSegment StartX=-4.3 StartY=3 StartZ=0 EndX=-7.3 EndY=3 EndZ=0
    g3: LineSegment StartX=-7.3 StartY=3 StartZ=0 EndX=-7.3 EndY=0 EndZ=0
  constraints (11):
    c: Coincident(g0,g1)
    c: Coincident(g1,g2)
    c: Coincident(g2,g3)
    c: Coincident(g3,g0)
    c: Horizontal(g0)
    c: Horizontal(g2)
    c: Vertical(g1)
    c: Vertical(g3)
    c: Coincident(g0,g-4)
    c: PointOnObject(g1,g-3)
    c: DistanceX(g2,g2) = 3
FEATURE [PartDesign::Pad] Pad246
  BaseFeature = -> Pocket093
  Direction = (-1,0,0)
  Length = 0.05
  Length2 = 10
  Profile = -> Sketch342
  ReferenceAxis = -> Sketch342 [N_Axis]
  Refine = true
  Suppressed = false
  Type = 0
FEATURE [Sketcher::SketchObject] Sketch343
  ArcFitTolerance = 1e-06
  AttachmentSupport = -> [Pad246]
  ExternalGeometry = -> [Pad246]
  FullyConstrained = true
  MakeInternals = false
  MapMode = 5
  Placement = pos=(8.1,0,0) rot=(0.57735,0.57735,0.57735;2.0944rad)
  sketch-geometry (4):
    g0: LineSegment StartX=7.3 StartY=0 StartZ=0 EndX=7.3 EndY=3 EndZ=0
    g1: LineSegment StartX=7.3 StartY=3 StartZ=0 EndX=4.3 EndY=3 EndZ=0
    g2: LineSegment StartX=4.3 StartY=3 StartZ=0 EndX=4.3 EndY=0 EndZ=0
    g3: LineSegment StartX=4.3 StartY=0 StartZ=0 EndX=7.3 EndY=0 EndZ=0
  constraints (11):
    c: Coincident(g0,g1)
    c: Coincident(g1,g2)
    c: Coincident(g2,g3)
    c: Coincident(g3,g0)
    c: Vertical(g0)
    c: Vertical(g2)
    c: Horizontal(g1)
    c: Horizontal(g3)
    c: Coincident(g0,g-4)
    c: PointOnObject(g1,g-3)
    c: DistanceX(g1,g1) = 3
FEATURE [PartDesign::Pad] Pad247
  BaseFeature = -> Pad246
  Direction = (1,0,0)
  Length = 0.05
  Length2 = 10
  Profile = -> Sketch343
  ReferenceAxis = -> Sketch343 [N_Axis]
  Refine = true
  Suppressed = false
  Type = 0
FEATURE [PartDesign::Body] Body013  label="Main_Head"
  AllowCompound = false
  Group = -> [Sketch190,Pad127,Sketch191,Pad128,Sketch192,Pad129,Sketch193,Pad130,Pocket088,Pad131,Pad132,Sketch195,Pad133,Sketch196,Pad134,Sketch197,Pad135,Sketch198,Pad136,Sketch199,Pocket089,Sketch200,Pad137,Sketch201,Pocket090,Sketch202,Pad138,Sketch203,Pocket091,Sketch204,Pocket092,Sketch205,Pad139,Fillet008,Sketch206,Pocket093,Sketch342,Pad246,Sketch343,Pad247]
  Origin = -> Origin013
  Placement = pos=(22,48.5,-4) rot=(0,0,1;3.14159rad)
  Tip = -> Pad247
FEATURE [Sketcher::SketchObject] Sketch344
  ArcFitTolerance = 1e-06
  AttachmentSupport = -> [Pocket095]
  ExternalGeometry = -> [Pocket095]
  FullyConstrained = true
  MakeInternals = false
  MapMode = 5
  Placement = pos=(0,0,-6.3) rot=(1,0,0;3.14159rad)
  sketch-geometry (4):
    g0: LineSegment StartX=18.3 StartY=-42.2 StartZ=0 EndX=18.3 EndY=-42.1 EndZ=0
    g1: LineSegment StartX=18.3 StartY=-42.1 StartZ=0 EndX=17.7 EndY=-42.1 EndZ=0
    g2: LineSegment StartX=17.7 StartY=-42.1 StartZ=0 EndX=17.7 EndY=-42.2 EndZ=0
    g3: LineSegment StartX=17.7 StartY=-42.2 StartZ=0 EndX=18.3 EndY=-42.2 EndZ=0
  constraints (10):
    c: Coincident(g0,g1)
    c: Coincident(g1,g2)
    c: Coincident(g2,g3)
    c: Coincident(g3,g0)
    c: Vertical(g0)
    c: Vertical(g2)
    c: Horizontal(g1)
    c: Horizontal(g3)
    c: Coincident(g0,g-4)
    c: Coincident(g1,g-3)
FEATURE [PartDesign::Pocket] Pocket161
  BaseFeature = -> Pocket095
  Direction = (0,0,1)
  Length = 0.2
  Length2 = 5
  Profile = -> Sketch344
  ReferenceAxis = -> Sketch344 [N_Axis]
  Refine = true
  Suppressed = false
  Type = 0
FEATURE [PartDesign::Body] Body014  label="Face"
  AllowCompound = false
  Group = -> [Binder008,Sketch207,Pad140,Sketch208,Pocket094,Sketch209,Pad141,Sketch210,Pad142,Sketch211,Pad143,Sketch212,Pocket095,Sketch344,Pocket161]
  Origin = -> Origin015
  Tip = -> Pocket161
PROVENANCE & LICENSES
A FreeCAD (.FCStd) document from a public repository crawl; recipes are the document's own serialized feature recipes (and, for linked parts, companion documents' recipes).
License: as declared in the source repository (recorded in the dataset sidecar).
